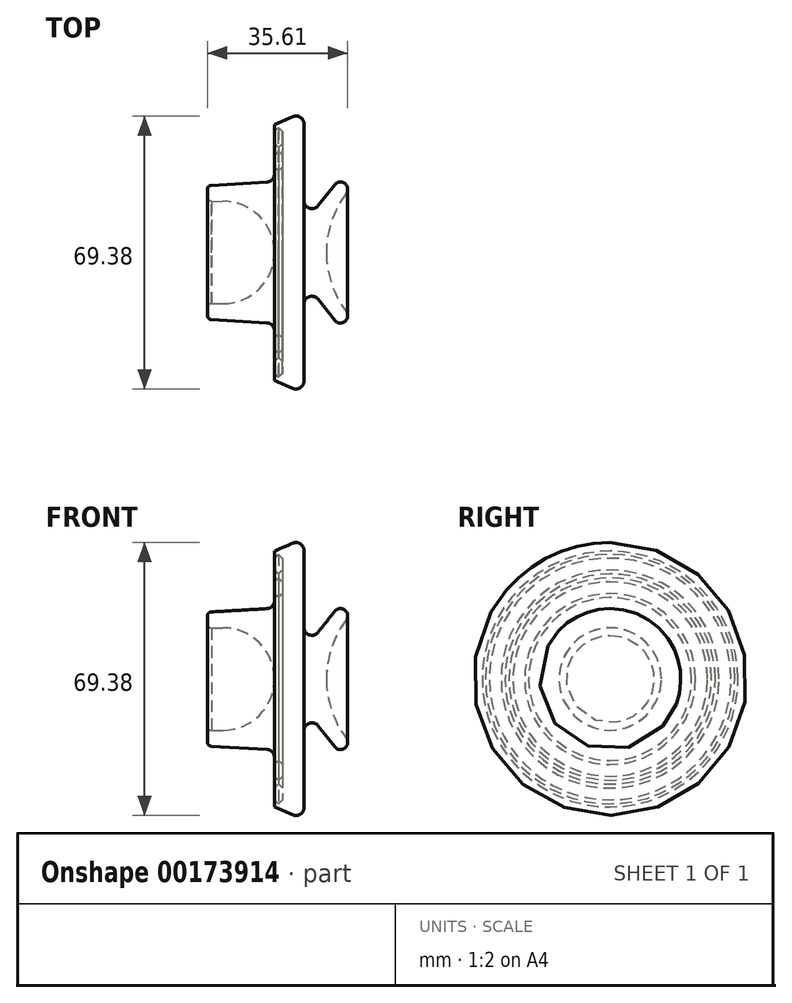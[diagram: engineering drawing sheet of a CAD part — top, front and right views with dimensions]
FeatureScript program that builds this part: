
annotation { "Feature Type Name" : "Feature", "Feature Type Description" : "" }
export const myFeature = defineFeature(function(context is Context, id is Id, definition is map)
    precondition{}
    {
        {
            var Q0;
            Q0=qCreatedBy(makeId("Front.planeOp"),FACE);
            var sketch = newSketch(context, id + "F0", { "sketchPlane" : qUnion([Q0])});
            skLineSegment(sketch, "E0", {"start": v(-19.29, 18) * mm, "end": v(22.9, 18) * mm, "construction": true});
            skLineSegment(sketch, "E1", {"start": v(0, 30.7) * mm, "end": v(0, 32.5) * mm});
            skLineSegment(sketch, "E2", {"start": v(7.5, 32.69) * mm, "end": v(7.5, 13.11) * mm});
            skLineSegment(sketch, "E3", {"start": v(-1.88, 17.89) * mm, "end": v(-16.06, 17.06) * mm});
            skLineSegment(sketch, "E4", {"start": v(-17, 16.06) * mm, "end": v(-17, 13.99) * mm});
            skLineSegment(sketch, "E5", {"start": v(-17, 13) * mm, "end": v(0, 13) * mm, "construction": true});
            skPoint(sketch, "E6.visualSharp", {"position": v(0, 18) * mm});
            skArc(sketch, "E6.filletArc", {"start": v(-1.88, 17.89) * mm, "mid": v(-0.54, 18.51) * mm, "end": v(0, 19.89) * mm});
            skLineSegment(sketch, "E7", {"start": v(4.71, 34.52) * mm, "end": v(0, 32.5) * mm});
            skPoint(sketch, "E8.visualSharp", {"position": v(7.5, 35.72) * mm});
            skArc(sketch, "E8.filletArc", {"start": v(7.5, 32.69) * mm, "mid": v(6.6, 34.36) * mm, "end": v(4.71, 34.52) * mm});
            skPoint(sketch, "E9.visualSharp", {"position": v(-17, 17) * mm});
            skArc(sketch, "E9.filletArc", {"start": v(-16.06, 17.06) * mm, "mid": v(-16.73, 16.74) * mm, "end": v(-17, 16.06) * mm});
            skPoint(sketch, "E10.visualSharp", {"position": v(-17, 13) * mm});
            skArc(sketch, "E10.filletArc", {"start": v(-17, 13.99) * mm, "mid": v(-16.72, 13.29) * mm, "end": v(-16.02, 12.99) * mm});
            skLineSegment(sketch, "E11", {"start": v(11.06, 11.87) * mm, "end": v(15.36, 17.25) * mm});
            skLineSegment(sketch, "E12", {"start": v(16.9, 18) * mm, "end": v(16.92, 18) * mm});
            skPoint(sketch, "E13.newPointB", {"position": v(7.5, 0) * mm});
            skArc(sketch, "E13.filletArc", {"start": v(7.5, 13.11) * mm, "mid": v(8.84, 11.23) * mm, "end": v(11.06, 11.87) * mm});
            skArc(sketch, "E14", {"start": v(15.36, 17.25) * mm, "mid": v(17.9, 17.55) * mm, "end": v(18.24, 15.01) * mm});
            skLineSegment(sketch, "E15", {"start": v(13.22, 0) * mm, "end": v(13.22, -6.35) * mm, "construction": true});
            skArc(sketch, "E16", {"start": v(13.22, 0) * mm, "mid": v(14.5, 7.92) * mm, "end": v(18.24, 15.01) * mm});
            skLineSegment(sketch, "E17", {"start": v(0, 30.7) * mm, "end": v(1, 31.7) * mm});
            skLineSegment(sketch, "E18", {"start": v(1, 31.7) * mm, "end": v(2, 30.7) * mm});
            skLineSegment(sketch, "E19", {"start": v(2, 30.7) * mm, "end": v(2, 27.7) * mm});
            skLineSegment(sketch, "E20", {"start": v(2, 21.7) * mm, "end": v(1, 20.7) * mm});
            skLineSegment(sketch, "E21", {"start": v(1, 20.7) * mm, "end": v(0, 21.7) * mm});
            skLineSegment(sketch, "E22", {"start": v(0, 0) * mm, "end": v(13.22, 0) * mm});
            skLineSegment(sketch, "E23", {"start": v(0, 21.7) * mm, "end": v(0, 19.89) * mm});
            skLineSegment(sketch, "E24", {"start": v(2, 27.7) * mm, "end": v(1, 26.7) * mm});
            skLineSegment(sketch, "E25", {"start": v(1, 26.7) * mm, "end": v(0, 27.7) * mm});
            skLineSegment(sketch, "E26", {"start": v(0, 27.7) * mm, "end": v(0, 24.7) * mm});
            skLineSegment(sketch, "E27", {"start": v(0, 24.7) * mm, "end": v(1, 25.7) * mm});
            skLineSegment(sketch, "E28", {"start": v(1, 25.7) * mm, "end": v(2, 24.7) * mm});
            skLineSegment(sketch, "E29.trimOffspring", {"start": v(2, 24.7) * mm, "end": v(2, 21.7) * mm});
            skLineSegment(sketch, "E30", {"start": v(0, 0) * mm, "end": v(0, -9.63) * mm, "construction": true});
            skArc(sketch, "E31", {"start": v(0, 0) * mm, "mid": v(-3.8, 9.2) * mm, "end": v(-13, 13) * mm});
            skLineSegment(sketch, "E32", {"start": v(-16.02, 12.99) * mm, "end": v(-13, 13) * mm});
            skSolve(sketch);
        }
        {
            var Q0;
            Q0=makeQuery(id+"F0.imprint","IMPRINT",FACE,{"disambiguationData":[TD([[makeQuery(id+"F0.imprint","IMPRINT",EDGE,{"derivedFrom":sQuery(id+"F0.wireOp",EDGE,"E1")}),-1.0]])]});
            var Q1;
            Q1=sQuery(id+"F0.wireOp",EDGE,"E22");
            revolve(context, id + "F1", {"entities" : qUnion([Q0]), "axis" : qUnion([Q1]), "revolveType" : RevolveType.FULL});
        }
    });
